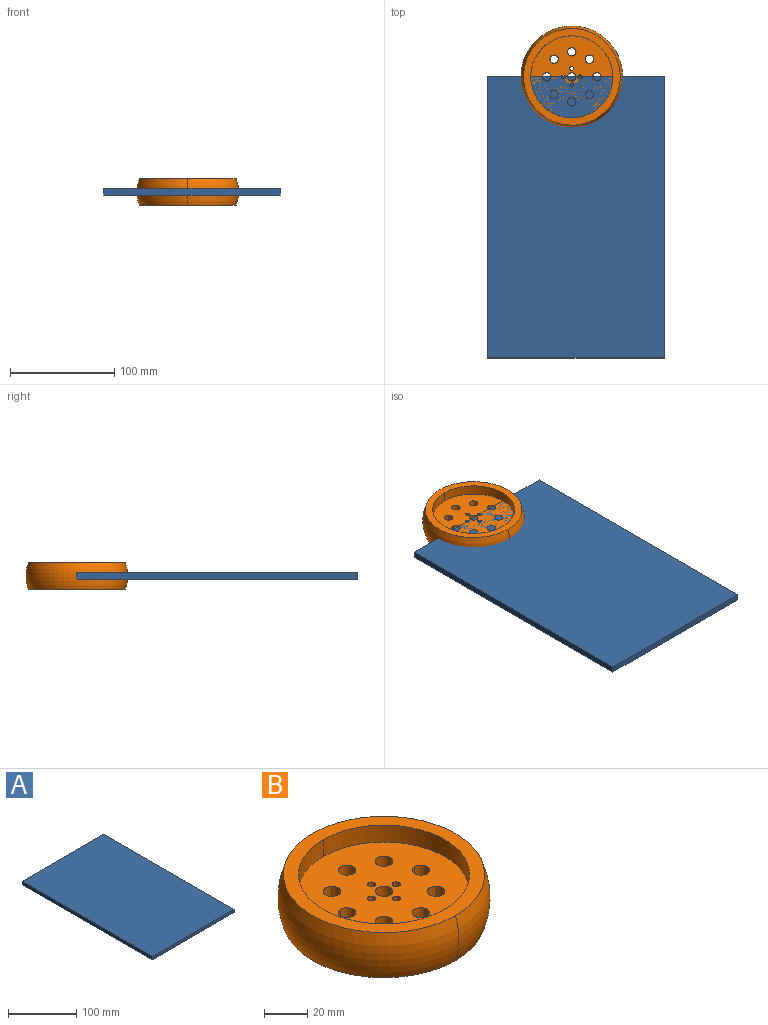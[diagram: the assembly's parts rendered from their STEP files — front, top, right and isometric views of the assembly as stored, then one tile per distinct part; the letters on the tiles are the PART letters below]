
ASSEMBLY  parts=2 mates=1
PART A: 6 faces, bbox 169.5x269.6x6.1 mm
  f0: plane 269.6x6.1mm, normal (1,0,0), area 1643.5mm2, adj f1,f3,f4,f5
  f1: plane 169.49x6.1mm, normal (0,1,0), area 1033.2mm2, adj f0,f2,f4,f5
  f2: plane 269.6x6.1mm, normal (-1,0,0), area 1643.5mm2, adj f1,f3,f4,f5
  f3: plane 169.49x6.1mm, normal (0,-1,0), area 1033.2mm2, adj f0,f2,f4,f5
  f4: plane 269.6x169.49mm, normal (0,0,1), area 45695.4mm2, adj f0,f1,f2,f3
  f5: plane 269.6x169.49mm, normal (0,0,-1), area 45695.4mm2, adj f0,f1,f2,f3
PART B: 36 faces, bbox 97.6x97.6x25.4 mm
  f0: cylinder r=39.37mm len=78.74mm, axis (0,0,1), area 1178.1mm2, adj f1,f2,f3
  f1: cylinder r=39.37mm len=78.74mm, axis (0,0,1), area 1178.1mm2, adj f0,f2,f3
  f2: plane 92.72x92.68mm, normal (0,0,1), area 1876.5mm2, adj f0,f1,f4,f5
  f3: plane 78.78x78.74mm, normal (0,0,1), area 4374.1mm2, adj f0,f1,f6,f7,f8,f9,f10,f11
  f4: revolved ~97.6x48.8mm, area 3923.4mm2, adj f2,f5,f32
  f5: revolved ~97.6x48.8mm, area 3923.4mm2, adj f2,f4,f32
  f6: cylinder r=4mm len=8mm, axis (0,0,1), area 79.8mm2, adj f3,f7,f34
  f7: cylinder r=4mm len=8mm, axis (0,0,1), area 79.8mm2, adj f3,f6,f34
  f8: cylinder r=1.85mm len=6.35mm, axis (0,0,1), area 36.9mm2, adj f3,f9,f34
  f9: cylinder r=1.85mm len=6.35mm, axis (0,0,1), area 36.9mm2, adj f3,f8,f34
  f10: cylinder r=1.85mm len=6.35mm, axis (0,0,1), area 36.9mm2, adj f3,f11,f34
  f11: cylinder r=1.85mm len=6.35mm, axis (0,0,1), area 36.9mm2, adj f3,f10,f34
  f12: cylinder r=1.85mm len=6.35mm, axis (0,0,1), area 36.9mm2, adj f3,f13,f34
  f13: cylinder r=1.85mm len=6.35mm, axis (0,0,1), area 36.9mm2, adj f3,f12,f34
  f14: cylinder r=1.85mm len=6.35mm, axis (0,0,1), area 36.9mm2, adj f3,f15,f34
  f15: cylinder r=1.85mm len=6.35mm, axis (0,0,1), area 36.9mm2, adj f3,f14,f34
  f16: cylinder r=4mm len=8mm, axis (0,0,-1), area 79.8mm2, adj f3,f17,f34
  f17: cylinder r=4mm len=8mm, axis (0,0,-1), area 79.8mm2, adj f3,f16,f34
  f18: cylinder r=4mm len=6.83mm, axis (0,0,-1), area 79.8mm2, adj f3,f19,f34
  f19: cylinder r=4mm len=6.83mm, axis (0,0,-1), area 79.8mm2, adj f3,f18,f34
  f20: cylinder r=4mm len=8mm, axis (0,0,-1), area 79.8mm2, adj f3,f21,f34
  f21: cylinder r=4mm len=8mm, axis (0,0,-1), area 79.8mm2, adj f3,f20,f34
  f22: cylinder r=4mm len=6.83mm, axis (0,0,-1), area 79.8mm2, adj f3,f23,f34
  f23: cylinder r=4mm len=6.83mm, axis (0,0,-1), area 79.8mm2, adj f3,f22,f34
  f24: cylinder r=4mm len=8mm, axis (0,0,-1), area 79.8mm2, adj f3,f25,f34
  f25: cylinder r=4mm len=8mm, axis (0,0,-1), area 79.8mm2, adj f3,f24,f34
  f26: cylinder r=4mm len=6.83mm, axis (0,0,-1), area 79.8mm2, adj f3,f27,f34
  f27: cylinder r=4mm len=6.83mm, axis (0,0,-1), area 79.8mm2, adj f3,f26,f34
  f28: cylinder r=4mm len=8mm, axis (0,0,-1), area 79.8mm2, adj f3,f29,f34
  f29: cylinder r=4mm len=8mm, axis (0,0,-1), area 79.8mm2, adj f3,f28,f34
  f30: cylinder r=4mm len=6.83mm, axis (0,0,-1), area 79.8mm2, adj f3,f31,f34
  f31: cylinder r=4mm len=6.83mm, axis (0,0,-1), area 79.8mm2, adj f3,f30,f34
  f32: plane 92.72x92.68mm, normal (0,0,-1), area 1876.5mm2, adj f4,f5,f33,f35
  f33: cylinder r=39.37mm len=78.74mm, axis (0,0,1), area 1178.1mm2, adj f32,f34,f35
  f34: plane 78.78x78.74mm, normal (0,0,-1), area 4374.1mm2, adj f6,f7,f8,f9,f10,f11,f12,f13
  f35: cylinder r=39.37mm len=78.74mm, axis (0,0,1), area 1178.1mm2, adj f32,f33,f34
PLACE A t=(-227.28,-29.79,-41.93)mm
PLACE B t=(-231.28,105.02,-39.01)mm
MATE fastened B.f3 <-> A.f4  axis (0,0,1) through (-227.28,105.02,-35.83)mm
